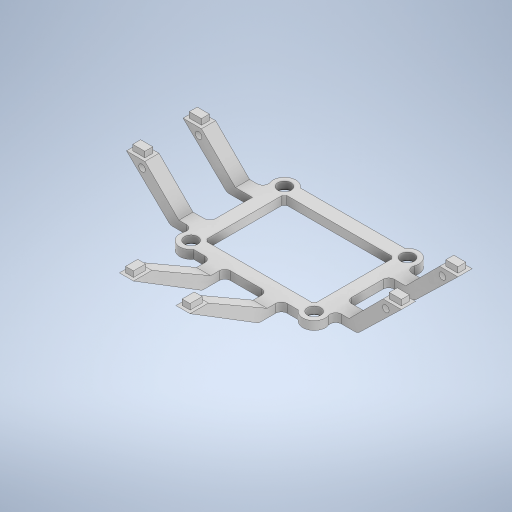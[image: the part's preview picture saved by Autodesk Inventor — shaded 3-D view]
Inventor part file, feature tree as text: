
AUTODESK INVENTOR PART (.ipt)
format: ipt  version: 2024.2 (Build 282272000, 272)  size: 483,328 bytes
history: native  units: mm
features: extrude x6, sketch x6, mirror x5, plane x4, fillet x2, chamfer x1
ambient origin geometry x8: Origin, YZ Plane, XZ Plane, XY Plane, X Axis, Y Axis, Z Axis, Center Point
bodies: Solid1 (feature_tree)
feature tree (24):
  extrude  "Extrusion1"  Depth=8.0mm
  chamfer  "Chamfer1"  Distance=8.0mm
  plane  "Work Plane2"
  extrude  "Extrusion2"  Depth=4.0mm
  plane  "Work Plane4"
  plane  "Work Plane5"
  mirror  "Mirror1"
  mirror  "Mirror2"
  plane  "Work Plane6"
  extrude  "Extrusion5"  Depth=4.0mm
  mirror  "Mirror5"
  extrude  "Extrusion4"  Depth=4.0mm
  mirror  "Mirror3"
  mirror  "Mirror4"
  extrude  "Extrusion6"  Depth=4.0mm
  fillet  "Fillet1"  Radius=4.0mm
  fillet  "Fillet2"  Radius=4.0mm
  extrude  "Extrusion8"  Depth=4.0mm
  sketch  "Sketch1"  dims[d0=4.7mm d1=8.0mm]
  sketch  "Sketch2"  dims[d2=4.7mm]
  sketch  "Sketch5"  dims[d3=8.0mm]
  sketch  "Sketch7"  dims[d4=4.7mm]
  sketch  "Sketch8"  dims[d5=8.0mm]
  sketch  "Sketch11"  dims[d6=4.7mm d7=8.0mm d8=4.0mm d9=4.0mm d10=4.0mm d11=4.0mm d12=4.0mm d13=4.0mm d14=4.0mm d15=4.0mm d16=33.0mm d17=4.7mm d18=4.7mm d19=4.7mm d20=4.7mm d21=2.35mm d22=2.35mm d23=2.35mm d24=2.35mm d25=43.5mm d26=3.0mm d27=0.0mm d28=0.5mm d29=2.0mm d30=45.0deg d32=4.0mm d41=5.0mm d42=0.0mm d47=21.75mm d48=16.5mm d49=6.5mm d61=9.0mm d62=4.3mm d63=2.8mm d64=1.1mm d65=1.1mm d66=2.0mm d67=0.0mm d71=9.25mm d72=8.0mm d73=6.5mm d76=5.0mm d77=0.0mm d78=2.8mm d79=4.3mm d80=2.8mm d81=4.3mm d82=1.1mm d83=1.1mm d84=1.1mm d85=1.1mm d86=2.0mm d87=0.0mm d91=6.0mm d93=45.0deg d94=15.0mm d95=15.0mm d96=2.0mm d97=2.0mm d98=5.0mm d99=30.0deg d105=2.3mm d106=2.5mm d107=5.5mm d108=2.3mm d109=2.5mm d110=5.5mm d111=0.0mm d112=0.0mm]
